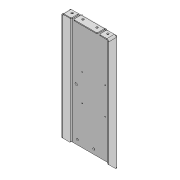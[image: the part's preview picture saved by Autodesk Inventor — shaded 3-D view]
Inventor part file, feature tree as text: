
AUTODESK INVENTOR PART (.ipt)
format: ipt  version: 2020 (Build 240168000, 168)  size: 237,568 bytes
history: native  units: mm
features: other x14, sketch x9, hole x4, projected_geometry x4, extrude x1, chamfer x1, fillet x1
ambient origin geometry x8: Origin, YZ Plane, XZ Plane, XY Plane, X Axis, Y Axis, Z Axis, Center Point
bodies: Body1 (feature_tree)
feature tree (34):
  other  "ソリッド1"
  other  "フランジ1"
  other  "フランジ5"
  extrude  "押し出し1"  Depth=100.0mm
  other  "フランジ6"
  hole  "穴1"  [1 undecoded]
  chamfer  "面取り1"  Distance=242.0mm
  fillet  "フィレット1"  Radius=2.0mm
  hole  "穴2"  [1 undecoded]
  hole  "穴3"  [1 undecoded]
  hole  "穴4"  [1 undecoded]
  sketch  "スケッチ1"
  other  "プレート1"
  sketch  "スケッチ2"
  other  "プレート2"
  other  "曲げ1"
  other  "コーナー1"
  sketch  "スケッチ6"
  other  "プレート6"
  other  "曲げ5"
  other  "コーナー5"
  sketch  "スケッチ7"
  sketch  "スケッチ8"
  other  "プレート7"
  other  "曲げ6"
  other  "コーナー6"
  sketch  "スケッチ9"
  sketch  "スケッチ10"
  projected_geometry  "投影ループ1"
  projected_geometry  "投影ループ2"
  projected_geometry  "投影ループ3"
  sketch  "スケッチ11"
  sketch  "スケッチ12"
  projected_geometry  "投影ループ4"
note: 4 required parameter values undecoded (feature->parameter linkage not recoverable at this tier; creation-order binding heuristic only, values carry confidence <= 0.55)
